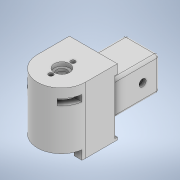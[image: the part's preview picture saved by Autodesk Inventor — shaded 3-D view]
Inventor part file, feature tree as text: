
AUTODESK INVENTOR PART (.ipt)
format: ipt  version: 2020.2 (Build 242310000, 310)  size: 447,488 bytes
history: native  units: mm
features: sketch x16, extrude x11, hole x5, fillet x4
ambient origin geometry x8: Origin, YZ Plane, XZ Plane, XY Plane, X Axis, Y Axis, Z Axis, Center Point
bodies: Solido1 (feature_tree)
feature tree (36):
  extrude  "Estrusione1"  Depth=18.0mm
  extrude  "Estrusione2"  Depth=40.0mm TaperAngle=0.0deg
  extrude  "Estrusione3"  Depth=46.0mm
  extrude  "Estrusione7"  Depth=37.0mm
  extrude  "Estrusione8"  Depth=21.0mm TaperAngle=0.0deg
  extrude  "Estrusione10"  Depth=22.5mm
  hole  "Foro4"  [1 undecoded]
  hole  "Foro5"  [1 undecoded]
  fillet  "Raccordo1"  Radius=46.0mm
  fillet  "Raccordo2"  Radius=37.0mm
  fillet  "Raccordo3"  Radius=37.0mm
  sketch  "Schizzo17"
  extrude  "Estrusione11"  Depth=14.0mm
  extrude  "Estrusione12"  TaperAngle=90.0deg  [1 undecoded]
  hole  "Foro6"  [1 undecoded]
  hole  "Foro7"  [1 undecoded]
  hole  "Foro8"  [1 undecoded]
  extrude  "Estrusione13"  Depth=14.0mm
  extrude  "Estrusione14"  TaperAngle=180.0deg  [1 undecoded]
  extrude  "Estrusione15"  TaperAngle=90.0deg  [1 undecoded]
  fillet  "Raccordo4"  Radius=21.0mm
  sketch  "Schizzo1"
  sketch  "Schizzo2"
  sketch  "Schizzo3"
  sketch  "Schizzo7"
  sketch  "Schizzo8"
  sketch  "Schizzo14"
  sketch  "Schizzo15"
  sketch  "Schizzo16"
  sketch  "Schizzo18"
  sketch  "Schizzo19"
  sketch  "Schizzo21"
  sketch  "Schizzo22"
  sketch  "Schizzo23"
  sketch  "Schizzo24"
  sketch  "Schizzo25"
note: 8 required parameter values undecoded (feature->parameter linkage not recoverable at this tier; creation-order binding heuristic only, values carry confidence <= 0.55)
